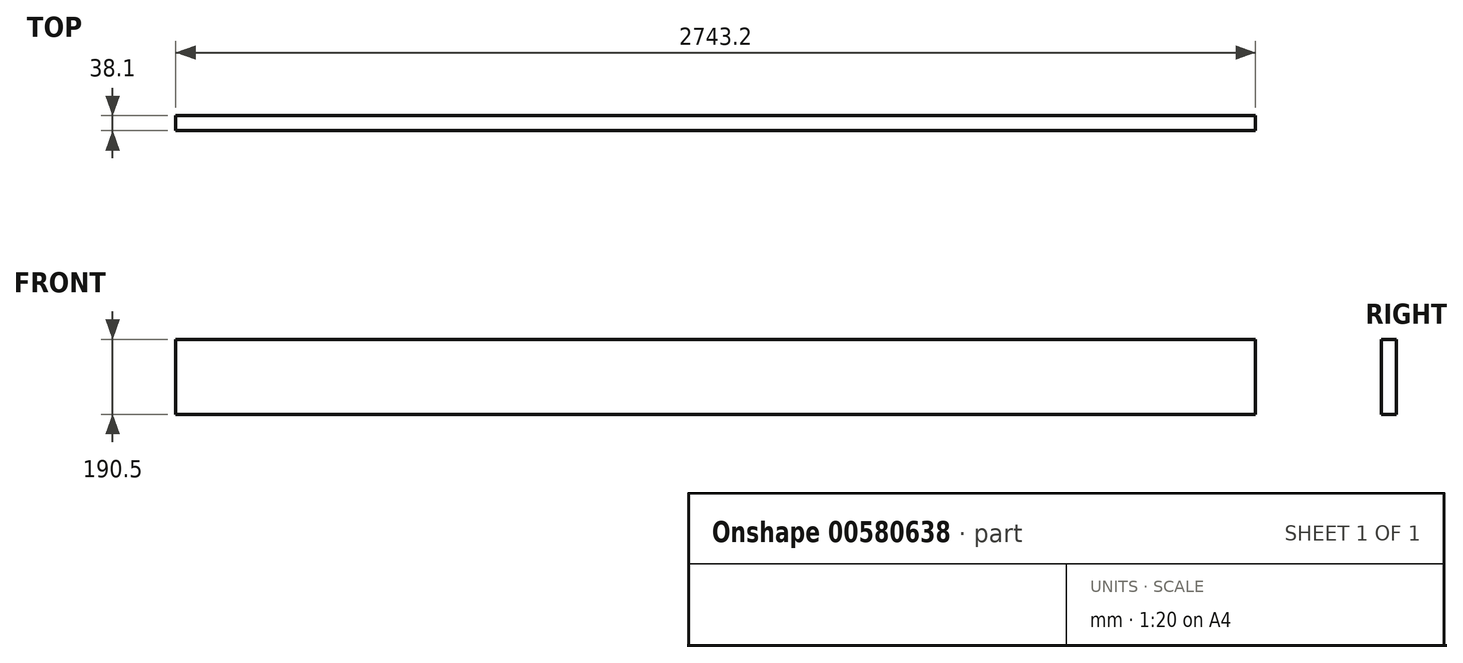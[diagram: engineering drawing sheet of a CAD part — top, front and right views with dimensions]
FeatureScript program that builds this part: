
annotation { "Feature Type Name" : "Feature", "Feature Type Description" : "" }
export const myFeature = defineFeature(function(context is Context, id is Id, definition is map)
    precondition{}
    {
        {
            var Q0;
            Q0=qCreatedBy(makeId("Top.planeOp"),FACE);
            var sketch = newSketch(context, id + "F0", { "sketchPlane" : qUnion([Q0])});
            skLineSegment(sketch, "E0.bottom", {"start": v(1371.6, -19.05) * mm, "end": v(-1371.6, -19.05) * mm});
            skLineSegment(sketch, "E0.top", {"start": v(1371.6, 19.05) * mm, "end": v(-1371.6, 19.05) * mm});
            skLineSegment(sketch, "E0.left", {"start": v(1371.6, -19.05) * mm, "end": v(1371.6, 19.05) * mm});
            skLineSegment(sketch, "E0.right", {"start": v(-1371.6, -19.05) * mm, "end": v(-1371.6, 19.05) * mm});
            skPoint(sketch, "E0.middle", {"position": v(0, 0) * mm});
            skSolve(sketch);
        }
        {
            var Q0;
            Q0=makeQuery(id+"F0.imprint","IMPRINT",FACE,{"disambiguationData":[TD([[makeQuery(id+"F0.imprint","IMPRINT",EDGE,{"derivedFrom":sQuery(id+"F0.wireOp",EDGE,"E0.bottom")}),-1.0]])]});
            extrude(context, id + "F1", {"entities" : qUnion([Q0]), "depth" : 190.5 * mm, "offsetDistance" : 25.4 * mm});
        }
    });
